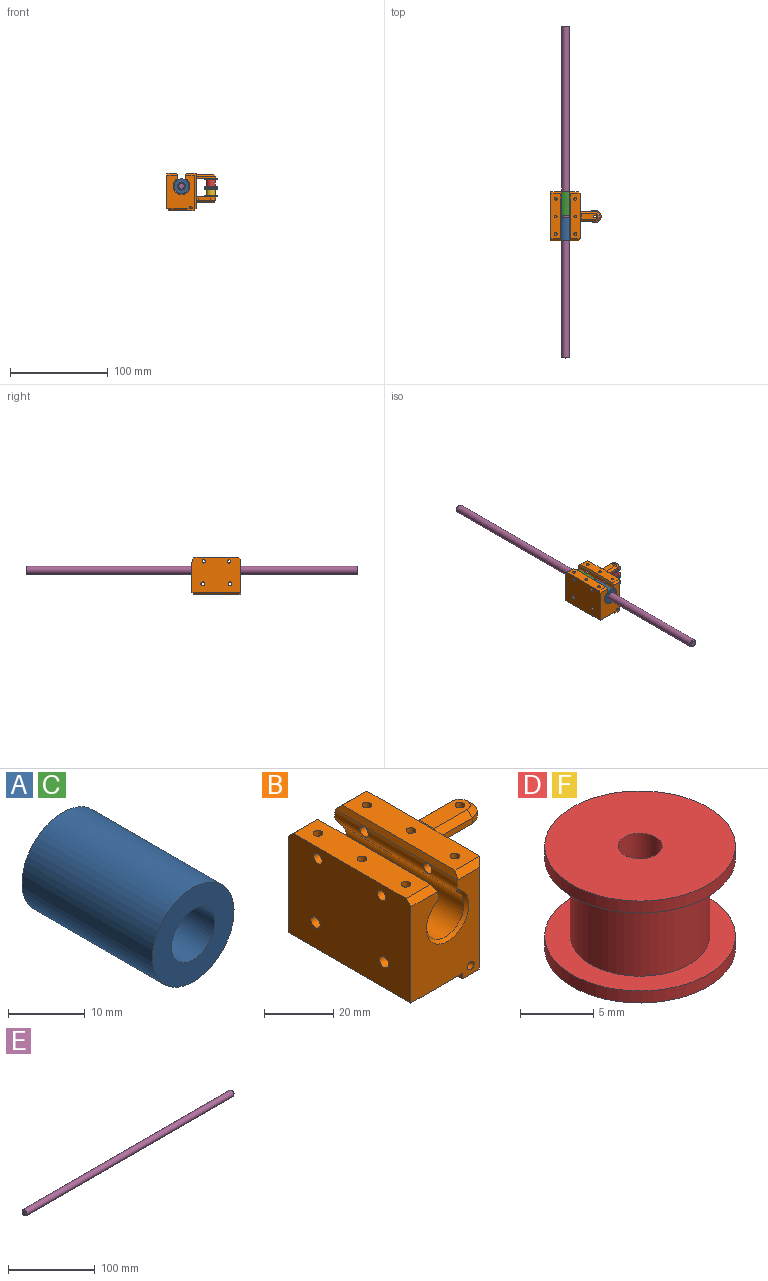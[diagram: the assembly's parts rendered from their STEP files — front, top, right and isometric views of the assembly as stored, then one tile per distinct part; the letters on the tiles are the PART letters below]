
ASSEMBLY  parts=6 mates=5
PART A: 4 faces, bbox 15x24x15 mm
  f0: cylinder r=4mm len=24mm, axis (0,1,0), area 603.2mm2, adj f2,f3
  f1: cylinder r=7.5mm len=24mm, axis (0,1,0), area 1131mm2, adj f2,f3
  f2: plane 15x15mm, normal (0,-1,0), area 126.4mm2, adj f0,f1
  f3: plane 15x15mm, normal (0,1,0), area 126.4mm2, adj f0,f1
PART B: 148 faces, bbox 50.5x50.5x38.7 mm
  f0: plane 46.47x36.47mm, normal (1,0,0), area 1219.5mm2, adj f18,f33,f34,f35,f36,f37,f38,f71
  f1: cylinder r=4.1mm len=19mm, axis (1,0,0), area 407mm2, adj f6,f7,f8,f9,f10,f24,f25,f36
  f2: cylinder r=1.7mm len=7.85mm, axis (1,0,0), area 83.8mm2, adj f5,f109
  f3: cylinder r=1.7mm len=7.85mm, axis (1,0,0), area 83.8mm2, adj f5,f102
  f4: cylinder r=5mm len=50mm, axis (0,1,0), area 270.1mm2, adj f19,f20,f30,f31,f39,f40,f94,f95
  f5: cylinder r=5mm len=50mm, axis (0,1,0), area 270.1mm2, adj f2,f3,f19,f20,f30,f32,f39,f40
  f6: plane 3.42x1.97mm, normal (1,0,0), area 1.3mm2, adj f1,f62
  f7: plane 3.42x1.97mm, normal (1,0,0), area 1.3mm2, adj f1,f63
  f8: plane 3.95x0.51mm, normal (1,0,0), area 1.3mm2, adj f1,f64
  f9: plane 3.42x1.97mm, normal (1,0,0), area 1.3mm2, adj f1,f65
  f10: plane 3.42x1.97mm, normal (1,0,0), area 1.3mm2, adj f1,f66
  f11: plane 3.95x1.14mm, normal (1,0,0), area 2.3mm2, adj f24,f25,f67
  f12: cylinder r=1.9mm len=6.5mm, axis (1,0,0), area 77.6mm2, adj f23,f68
  f13: plane 3.42x1.97mm, normal (1,0,0), area 1.3mm2, adj f27,f46
  f14: plane 3.95x0.51mm, normal (1,0,0), area 1.3mm2, adj f27,f47
  f15: plane 3.42x1.97mm, normal (1,0,0), area 1.3mm2, adj f27,f48
  f16: plane 3.42x1.97mm, normal (1,0,0), area 1.3mm2, adj f27,f49
  f17: plane 3.95x1.14mm, normal (1,0,0), area 2.3mm2, adj f26,f28,f50
  f18: plane 46.38x10.38mm, normal (0,0,1), area 441.4mm2, adj f0,f32,f70,f79,f89,f91,f93,f134
  f19: plane 34x28mm, normal (0,1,0), area 696mm2, adj f4,f5,f23,f31,f32,f39,f70,f71
  f20: plane 36x28mm, normal (0,-1,0), area 703.8mm2, adj f4,f5,f22,f23,f31,f32,f40,f76
  f21: plane 46x10mm, normal (0,0,1), area 441.5mm2, adj f23,f31,f80,f81,f83,f85,f87
  f22: plane 48x26mm, normal (0,0,-1), area 1196.8mm2, adj f20,f55,f72,f74,f75,f76,f111,f144
  f23: plane 50x36mm, normal (-1,0,0), area 1755.2mm2, adj f12,f19,f20,f21,f56,f74,f80,f81
  f24: plane 19x2.05mm, normal (0,-0.87,0.5), area 45mm2, adj f1,f11,f25,f38,f61
  f25: plane 19x2.05mm, normal (0,-0.87,-0.5), area 45mm2, adj f1,f11,f24,f37,f69
  f26: plane 19x2.05mm, normal (0,-0.87,-0.5), area 45mm2, adj f17,f27,f28,f35,f41
  f27: cylinder r=4.1mm len=19mm, axis (1,0,0), area 407.9mm2, adj f13,f14,f15,f16,f26,f28,f29,f34
  f28: plane 19x2.05mm, normal (0,-0.87,0.5), area 45mm2, adj f17,f26,f27,f33,f53
  f29: plane 3.42x1.97mm, normal (1,0,0), area 1.3mm2, adj f27,f51
  f30: cylinder r=7.65mm len=48mm, axis (0,1,0), area 1739.1mm2, adj f4,f5,f39,f40
  f31: plane 50x2.15mm, normal (0.93,0,0.36), area 111.1mm2, adj f4,f19,f20,f21,f80,f81
  f32: plane 50x2.15mm, normal (-0.93,0,0.36), area 111.1mm2, adj f5,f18,f19,f20,f70,f79
  f33: plane 2.55x2.34mm, normal (0.71,-0.61,0.35), area 3.8mm2, adj f0,f28,f34,f35
  f34: cone r=4.1mm half-angle=45deg, axis (1,0,0), area 34.1mm2, adj f0,f27,f33,f35
  f35: plane 2.55x2.34mm, normal (0.71,-0.61,-0.35), area 3.8mm2, adj f0,f26,f33,f34
  f36: cone r=5.1mm half-angle=45deg, axis (1,0,0), area 34.1mm2, adj f0,f1,f37,f38
  f37: plane 2.55x2.34mm, normal (0.71,-0.61,-0.35), area 3.8mm2, adj f0,f25,f36,f38
  f38: plane 2.55x2.34mm, normal (0.71,-0.61,0.35), area 3.8mm2, adj f0,f24,f36,f37
  f39: cone r=7.65mm half-angle=45deg, axis (0,1,0), area 58mm2, adj f4,f5,f19,f30
  f40: cone r=8.65mm half-angle=45deg, axis (0,-1,0), area 58mm2, adj f4,f5,f20,f30
  f41: plane 0.15x0.09mm, normal (-1,0,0), area 0mm2, adj f26,f27,f50,f51
  f42: plane 0.18x0.05mm, normal (-1,0,0), area 0mm2, adj f27,f46,f51
  f43: plane 0.15x0.09mm, normal (-1,0,0), area 0mm2, adj f27,f46,f47
  f44: plane 0.15x0.09mm, normal (-1,0,0), area 0mm2, adj f27,f47,f48
  f45: plane 0.18x0.05mm, normal (-1,0,0), area 0mm2, adj f27,f48,f49
  f46: plane 3.59x3.5mm, normal (0,0.5,-0.87), area 14.5mm2, adj f13,f42,f43,f47,f51,f52
  f47: plane 4.15x3.5mm, normal (0,1,0), area 14.5mm2, adj f14,f43,f44,f46,f48,f52
  f48: plane 3.59x3.5mm, normal (0,0.5,0.87), area 14.5mm2, adj f15,f44,f45,f47,f49,f52
  f49: plane 3.59x3.5mm, normal (0,-0.5,0.87), area 14.5mm2, adj f16,f45,f48,f50,f52,f53
  f50: plane 4.15x3.5mm, normal (0,-1,0), area 14.5mm2, adj f17,f41,f49,f51,f52,f53
  f51: plane 3.59x3.5mm, normal (0,-0.5,-0.87), area 14.5mm2, adj f29,f41,f42,f46,f50,f52
  f52: plane 8.3x7.19mm, normal (1,0,0), area 33.4mm2, adj f46,f47,f48,f49,f50,f51,f56
  f53: plane 0.15x0.09mm, normal (-1,0,0), area 0mm2, adj f27,f28,f49,f50
  f54: cone r=0mm half-angle=59deg, axis (0,0,-1), area 7.7mm2, adj f55
  f55: cylinder r=1.45mm len=8mm, axis (0,0,-1), area 72.9mm2, adj f22,f54
  f56: cylinder r=1.9mm len=6.5mm, axis (1,0,0), area 77.6mm2, adj f23,f52
  f57: plane 0.18x0.05mm, normal (-1,0,0), area 0mm2, adj f1,f65,f66
  f58: plane 0.15x0.09mm, normal (-1,0,0), area 0mm2, adj f1,f64,f65
  f59: plane 0.15x0.09mm, normal (-1,0,0), area 0mm2, adj f1,f63,f64
  f60: plane 0.18x0.05mm, normal (-1,0,0), area 0mm2, adj f1,f62,f63
  f61: plane 0.15x0.09mm, normal (-1,0,0), area 0mm2, adj f1,f24,f66,f67
  f62: plane 3.59x3.5mm, normal (0,-0.5,-0.87), area 14.5mm2, adj f6,f60,f63,f67,f68,f69
  f63: plane 3.59x3.5mm, normal (0,0.5,-0.87), area 14.5mm2, adj f7,f59,f60,f62,f64,f68
  f64: plane 4.15x3.5mm, normal (0,1,0), area 14.5mm2, adj f8,f58,f59,f63,f65,f68
  f65: plane 3.59x3.5mm, normal (0,0.5,0.87), area 14.5mm2, adj f9,f57,f58,f64,f66,f68
  f66: plane 3.59x3.5mm, normal (0,-0.5,0.87), area 14.5mm2, adj f10,f57,f61,f65,f67,f68
  f67: plane 4.15x3.5mm, normal (0,-1,0), area 14.5mm2, adj f11,f61,f62,f66,f68,f69
  f68: plane 8.3x7.19mm, normal (1,0,0), area 33.4mm2, adj f12,f62,f63,f64,f65,f66,f67
  f69: plane 0.15x0.09mm, normal (-1,0,0), area 0mm2, adj f1,f25,f62,f67
  f70: plane 10.77x2mm, normal (0,0.71,0.71), area 26.5mm2, adj f18,f19,f32,f71
  f71: plane 36x2mm, normal (0.71,0.71,0), area 99mm2, adj f0,f19,f70,f73
  f72: plane 28x2mm, normal (0,0.71,-0.71), area 76.4mm2, adj f19,f22,f73,f74
  f73: plane 2x2mm, normal (0.58,0.58,-0.58), area 3.5mm2, adj f71,f72,f75
  f74: plane 50x2mm, normal (-0.71,0,-0.71), area 135.8mm2, adj f22,f23,f72,f76
  f75: plane 46x2mm, normal (0.71,0,-0.71), area 130.1mm2, adj f0,f22,f73,f77
  f76: plane 21x2mm, normal (0,-0.71,-0.71), area 56.6mm2, adj f20,f22,f74,f145
  f77: plane 2x2mm, normal (0.58,-0.58,-0.58), area 3.5mm2, adj f75,f78,f144
  f78: plane 36x2mm, normal (0.71,-0.71,0), area 99mm2, adj f0,f20,f77,f79
  f79: plane 10.77x2mm, normal (0,-0.71,0.71), area 26.5mm2, adj f18,f20,f32,f78
  f80: plane 10.77x2mm, normal (0,-0.71,0.71), area 29.4mm2, adj f20,f21,f23,f31
  f81: plane 10.77x2mm, normal (0,0.71,0.71), area 29.4mm2, adj f19,f21,f23,f31
  f82: cone r=0mm half-angle=59deg, axis (0,0,1), area 7.2mm2, adj f83
  f83: cylinder r=1.4mm len=7mm, axis (0,0,1), area 61.6mm2, adj f21,f82
  f84: cone r=0mm half-angle=59deg, axis (0,0,1), area 7.2mm2, adj f85
  f85: cylinder r=1.4mm len=7mm, axis (0,0,1), area 61.6mm2, adj f21,f84
  f86: cone r=0mm half-angle=59deg, axis (0,0,1), area 7.2mm2, adj f87
  f87: cylinder r=1.4mm len=7mm, axis (0,0,1), area 61.6mm2, adj f21,f86
  f88: cone r=0mm half-angle=59deg, axis (0,0,1), area 7.2mm2, adj f89
  f89: cylinder r=1.4mm len=7mm, axis (0,0,1), area 61.6mm2, adj f18,f88
  f90: cone r=0mm half-angle=59deg, axis (0,0,1), area 7.2mm2, adj f91
  f91: cylinder r=1.4mm len=7mm, axis (0,0,1), area 61.6mm2, adj f18,f90
  f92: cone r=0mm half-angle=59deg, axis (0,0,1), area 7.2mm2, adj f93
  f93: cylinder r=1.4mm len=7mm, axis (0,0,1), area 61.6mm2, adj f18,f92
  f94: cylinder r=1.7mm len=10.85mm, axis (1,0,0), area 115.8mm2, adj f4,f23
  f95: cylinder r=1.7mm len=10.85mm, axis (1,0,0), area 115.8mm2, adj f4,f23
  f96: plane 3x3mm, normal (0,-0.87,-0.5), area 10.4mm2, adj f0,f97,f101,f102
  f97: plane 3.46x3mm, normal (0,0,-1), area 10.4mm2, adj f0,f96,f98,f102
  f98: plane 3x3mm, normal (0,0.87,-0.5), area 10.4mm2, adj f0,f97,f99,f102
  f99: plane 3x3mm, normal (0,0.87,0.5), area 10.4mm2, adj f0,f98,f100,f102
  f100: plane 3.46x3mm, normal (0,0,1), area 10.4mm2, adj f0,f99,f101,f102
  f101: plane 3x3mm, normal (0,-0.87,0.5), area 10.4mm2, adj f0,f96,f100,f102
  f102: plane 6.93x6mm, normal (1,0,0), area 22.1mm2, adj f3,f96,f97,f98,f99,f100,f101
  f103: plane 3x3mm, normal (0,0.87,-0.5), area 10.4mm2, adj f0,f104,f108,f109
  f104: plane 3x3mm, normal (0,0.87,0.5), area 10.4mm2, adj f0,f103,f105,f109
  f105: plane 3.46x3mm, normal (0,0,1), area 10.4mm2, adj f0,f104,f106,f109
  f106: plane 3x3mm, normal (0,-0.87,0.5), area 10.4mm2, adj f0,f105,f107,f109
  f107: plane 3x3mm, normal (0,-0.87,-0.5), area 10.4mm2, adj f0,f106,f108,f109
  f108: plane 3.46x3mm, normal (0,0,-1), area 10.4mm2, adj f0,f103,f107,f109
  f109: plane 6.93x6mm, normal (1,0,0), area 22.1mm2, adj f2,f103,f104,f105,f106,f107,f108
  f110: cone r=0mm half-angle=59deg, axis (0,0,-1), area 7.7mm2, adj f1,f111
  f111: cylinder r=1.45mm len=8mm, axis (0,0,-1), area 72.9mm2, adj f1,f22,f110
  f112: plane 18.5x10.13mm, normal (0,0,1), area 168.1mm2, adj f113,f115,f121,f125,f126,f129,f136
  f113: plane 13x4mm, normal (0,-1,0), area 52mm2, adj f112,f121,f122,f129
  f114: plane 16x6mm, normal (0,0,-1), area 86mm2, adj f122,f123,f124,f125,f128
  f115: plane 13x4mm, normal (0,1,0), area 52mm2, adj f112,f121,f124,f126
  f116: plane 13.5x2mm, normal (0,-1,0), area 27mm2, adj f117,f120,f132,f139
  f117: plane 18.5x10mm, normal (0,0,-1), area 168.1mm2, adj f116,f118,f120,f131,f133
  f118: plane 13.5x2mm, normal (0,1,0), area 27mm2, adj f117,f120,f135,f141
  f119: plane 16.59x6mm, normal (0,0,1), area 89.5mm2, adj f131,f134,f138,f139,f140,f141,f142
  f120: cylinder r=5mm len=10mm, axis (0,0,1), area 31.4mm2, adj f116,f117,f118,f140
  f121: cylinder r=5mm len=10mm, axis (0,0,-1), area 62.8mm2, adj f112,f113,f115,f123
  f122: plane 13x2mm, normal (0,-0.71,-0.71), area 36.8mm2, adj f113,f114,f123,f130
  f123: cone r=3mm half-angle=45deg, axis (0,0,1), area 35.5mm2, adj f114,f121,f122,f124
  f124: plane 13x2mm, normal (0,0.71,-0.71), area 36.8mm2, adj f114,f115,f123,f127
  f125: cylinder r=1.4mm len=6mm, axis (0,0,1), area 52.8mm2, adj f112,f114
  f126: cylinder r=2mm len=6.33mm, axis (0,0,1), area 15.3mm2, adj f0,f112,f115,f127,f136
  f127: cylinder r=2mm len=4.59mm, axis (0,0.71,0.71), area 11.5mm2, adj f0,f124,f126,f128
  f128: cylinder r=2mm len=7.66mm, axis (0,1,0), area 21.5mm2, adj f0,f114,f127,f130
  f129: cylinder r=2mm len=6.33mm, axis (0,0,-1), area 15.3mm2, adj f0,f112,f113,f130,f136
  f130: cylinder r=2mm len=4.59mm, axis (0,-0.71,0.71), area 11.5mm2, adj f0,f122,f128,f129
  f131: cylinder r=1.4mm len=4mm, axis (0,0,1), area 35.2mm2, adj f117,f119
  f132: cylinder r=1.5mm len=6.23mm, axis (0,0,-1), area 8.6mm2, adj f0,f116,f133,f137,f138
  f133: cylinder r=1.5mm len=13mm, axis (0,1,0), area 27.1mm2, adj f0,f117,f132,f135
  f134: cylinder r=1.5mm len=11.23mm, axis (0,1,0), area 15.9mm2, adj f18,f119,f137,f143
  f135: cylinder r=1.5mm len=6.23mm, axis (0,0,1), area 8.6mm2, adj f0,f118,f133,f142,f143
  f136: cylinder r=1.5mm len=14mm, axis (0,-1,0), area 28.4mm2, adj f0,f112,f126,f129
  f137: bspline ~5.23x3.23mm, area 6.8mm2, adj f0,f18,f132,f134,f138
  f138: cone r=3.5mm half-angle=45deg, axis (0,0,1), area 0.2mm2, adj f119,f132,f137,f139
  f139: plane 13.5x2mm, normal (0,-0.71,0.71), area 38.2mm2, adj f116,f119,f138,f140
  f140: cone r=3mm half-angle=45deg, axis (0,0,-1), area 35.5mm2, adj f119,f120,f139,f141
  f141: plane 13.5x2mm, normal (0,0.71,0.71), area 38.2mm2, adj f118,f119,f140,f142
  f142: cone r=3.5mm half-angle=45deg, axis (0,0,1), area 0.2mm2, adj f119,f135,f141,f143
  f143: bspline ~5.23x3.23mm, area 6.8mm2, adj f0,f18,f134,f135,f142
  f144: plane 2x2mm, normal (1,0,0), area 2mm2, adj f20,f22,f77
  f145: plane 2x2mm, normal (-1,0,0), area 2mm2, adj f20,f22,f76
  f146: cone r=0mm half-angle=59deg, axis (0,-1,0), area 7.2mm2, adj f147
  f147: cylinder r=1.4mm len=8mm, axis (0,-1,0), area 70.4mm2, adj f20,f146
PART C: same geometry as A
PART D: 8 faces, bbox 13x13x8.5 mm
  f0: cylinder r=6.5mm len=13mm, axis (0,0,-1), area 40.8mm2, adj f1,f2
  f1: plane 13x13mm, normal (0,0,1), area 61.9mm2, adj f0,f3
  f2: plane 13x13mm, normal (0,0,-1), area 125.7mm2, adj f0,f7
  f3: cylinder r=4.75mm len=9.5mm, axis (0,0,-1), area 194mm2, adj f1,f6
  f4: cylinder r=6.5mm len=13mm, axis (0,0,-1), area 40.8mm2, adj f5,f6
  f5: plane 13x13mm, normal (0,0,1), area 125.7mm2, adj f4,f7
  f6: plane 13x13mm, normal (0,0,-1), area 61.9mm2, adj f3,f4
  f7: cylinder r=1.5mm len=8.5mm, axis (0,0,1), area 80.1mm2, adj f2,f5
PART E: 5 faces, bbox 340x8x8 mm
  f0: cylinder r=4mm len=338mm, axis (-1,0,0), area 8494.9mm2, adj f3,f4
  f1: plane 6x6mm, normal (1,0,0), area 28.3mm2, adj f4
  f2: plane 6x6mm, normal (-1,0,0), area 28.3mm2, adj f3
  f3: cone r=4mm half-angle=45deg, axis (1,0,0), area 31.1mm2, adj f0,f2
  f4: cone r=3mm half-angle=45deg, axis (-1,0,0), area 31.1mm2, adj f0,f1
PART F: same geometry as D
PLACE A t=(-15.26,-24.44,7.38)mm
PLACE B t=(-15.26,-23.44,1.38)mm
PLACE C t=(-15.26,1.56,7.38)mm
PLACE D t=(14.74,-23.44,6.38)mm
PLACE E rot(axis=(0.58,-0.58,-0.58),120deg) t=(-15.26,1.56,7.38)mm
PLACE F t=(14.74,-23.44,-3.12)mm
MATE revolute F.f0 <-> B.f125  axis (0,0,-1) through (14.74,-23.44,-3.12)mm
MATE fastened B.f39 <-> C.f1  axis (0,1,0) through (-15.26,1.56,7.38)mm
MATE fastened A.f1 <-> B.f40  axis (0,-1,0) through (-15.26,-48.44,7.38)mm
MATE slider E.f0 <-> C.f0  axis (0,1,0) through (-15.26,1.56,7.38)mm
MATE revolute D.f0 <-> B.f120  axis (0,0,1) through (14.74,-23.44,14.88)mm
